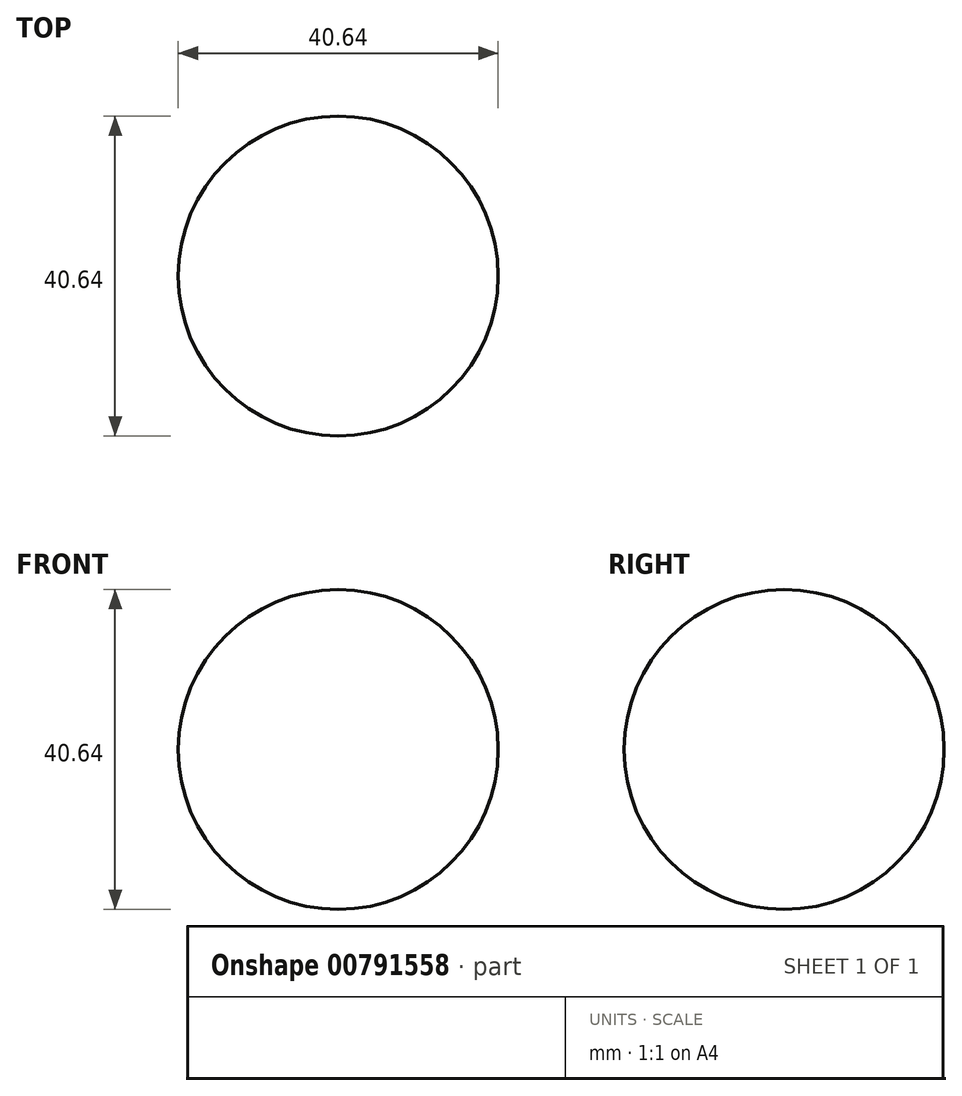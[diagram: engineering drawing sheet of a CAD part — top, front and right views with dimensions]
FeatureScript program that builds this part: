
annotation { "Feature Type Name" : "Feature", "Feature Type Description" : "" }
export const myFeature = defineFeature(function(context is Context, id is Id, definition is map)
    precondition{}
    {
        {
            var Q0;
            Q0=qCreatedBy(makeId("Front.planeOp"),FACE);
            var sketch = newSketch(context, id + "F0", { "sketchPlane" : qUnion([Q0])});
            skArc(sketch, "E0", {"start": v(0, 20.32) * mm, "mid": v(-20.32, 0) * mm, "end": v(0, -20.32) * mm});
            skLineSegment(sketch, "E1", {"start": v(0, 20.32) * mm, "end": v(0, -20.32) * mm});
            skSolve(sketch);
        }
        {
            var Q0;
            Q0 = qSketchRegion(id + "F0", true);
            var Q1;
            Q1=sQuery(id+"F0.wireOp",EDGE,"E1");
            revolve(context, id + "F1", {"surfaceOperationType" : NewSurfaceOperationType.NEW, "entities" : qUnion([Q0]), "axis" : qUnion([Q1]), "revolveType" : RevolveType.FULL});
        }
        {
            var Q0;
            Q0=qCreatedBy(makeId("Front.planeOp"),FACE);
            var sketch = newSketch(context, id + "F2", { "sketchPlane" : qUnion([Q0])});
            skCircle(sketch, "E2", {"center": v(0, 43.55) * mm, "radius": 1.27 * mm});
            skSolve(sketch);
        }
        {
            var Q0;
            Q0 = qSketchRegion(id + "F2", true);
            extrude(context, id + "F3", {"entities" : qUnion([Q0]), "operationType" : NewBodyOperationType.REMOVE, "depth" : 25.4 * mm, "offsetDistance" : 25.4 * mm, "hasSecondDirection" : true, "secondDirectionOppositeDirection" : true, "secondDirectionDepth" : 25.4 * mm});
        }
    });
